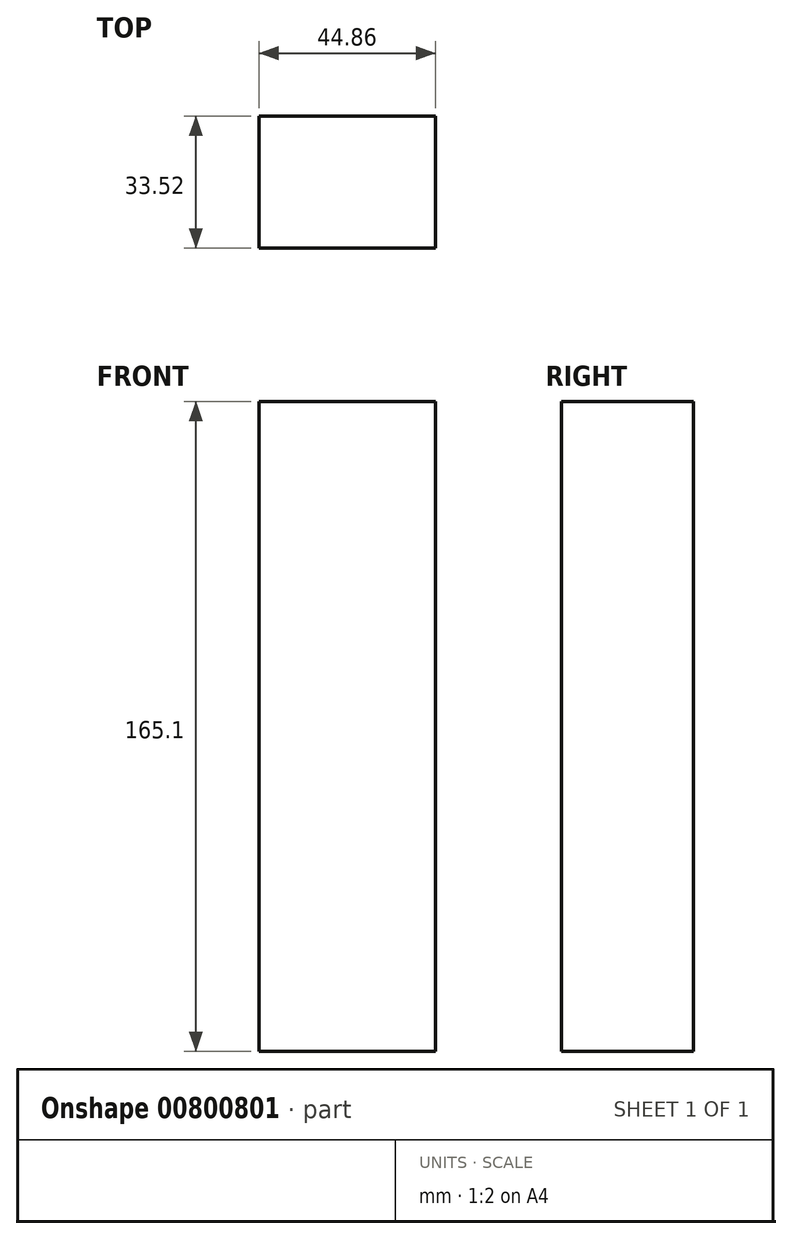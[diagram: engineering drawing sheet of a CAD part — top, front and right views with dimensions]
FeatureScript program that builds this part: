
annotation { "Feature Type Name" : "Feature", "Feature Type Description" : "" }
export const myFeature = defineFeature(function(context is Context, id is Id, definition is map)
    precondition{}
    {
        {
            var Q0;
            Q0=qCreatedBy(makeId("Front.planeOp"),FACE);
            var sketch = newSketch(context, id + "F0", { "sketchPlane" : qUnion([Q0])});
            skLineSegment(sketch, "E0.bottom", {"start": v(22.43, 82.55) * mm, "end": v(-22.43, 82.55) * mm});
            skLineSegment(sketch, "E0.top", {"start": v(22.43, -82.55) * mm, "end": v(-22.43, -82.55) * mm});
            skLineSegment(sketch, "E0.left", {"start": v(22.43, 82.55) * mm, "end": v(22.43, -82.55) * mm});
            skLineSegment(sketch, "E0.right", {"start": v(-22.43, 82.55) * mm, "end": v(-22.43, -82.55) * mm});
            skPoint(sketch, "E0.middle", {"position": v(0, 0) * mm});
            skSolve(sketch);
        }
        {
            var Q0;
            Q0=makeQuery(id+"F0.imprint","IMPRINT",FACE,{"disambiguationData":[TD([[makeQuery(id+"F0.imprint","IMPRINT",EDGE,{"derivedFrom":sQuery(id+"F0.wireOp",EDGE,"E0.bottom")}),1.0]])]});
            extrude(context, id + "F1", {"entities" : qUnion([Q0]), "endBound" : BoundingType.SYMMETRIC, "depth" : 33.53 * mm, "offsetDistance" : 25.4 * mm});
        }
    });
